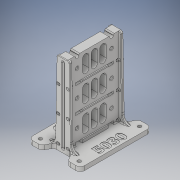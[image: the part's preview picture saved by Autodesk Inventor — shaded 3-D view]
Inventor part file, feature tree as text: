
AUTODESK INVENTOR PART (.ipt)
format: ipt  version: 2018.3 (Build 223284000, 284)  size: 1,960,960 bytes
history: native  units: in
note: dims shown in document units (in); Inventor stores cm internally (conversion verified against a paired STEP export)
features: extrude x12, sketch x11, fillet x9, mirror x4, chamfer x3, hole x2, emboss x2, pattern_linear x1, pattern_circular x1, revolve x1
ambient origin geometry x8: Origin, YZ Plane, XZ Plane, XY Plane, X Axis, Y Axis, Z Axis, Center Point
bodies: Solid1 (feature_tree)
feature tree (46):
  sketch  "Sketch1"  dims[d0=0.5in d1=3.0in]
  extrude  "Extrusion1"  Depth=3.0in
  sketch  "Sketch2"  dims[d2=4.779in d3=0.25in]
  extrude  "Extrusion2"  Depth=0.25in
  mirror  "Mirror1"
  hole  "Hole1"  [1 undecoded]
  extrude  "Extrusion3"  Depth=2.771in
  pattern_linear  "Rectangular Pattern1"  Count1=3 Spacing1=1.5in
  chamfer  "Chamfer1"  Distance=0.1562in
  fillet  "Fillet1"  Radius=1.0in
  extrude  "Extrusion4"  Depth=0.3937in
  extrude  "Extrusion5"  Depth=0.0625in TaperAngle=0.0deg
  chamfer  "Chamfer2"  Distance=1.1811in
  mirror  "Mirror2"
  fillet  "Fillet2"  Radius=0.0312in
  sketch  "Sketch3"  dims[d4=0.5in d5=3.125in d6=0.0in]
  sketch  "Sketch4"  dims[d7=2.0in d8=2.771in]
  extrude  "Extrusion6"  Depth=0.0625in
  extrude  "Extrusion9"  Depth=0.0625in
  hole  "Hole2"  [1 undecoded]
  fillet  "Fillet3"  Radius=0.1in
  extrude  "Extrusion7"  Depth=0.3937in
  extrude  "Extrusion8"  Depth=0.0625in
  mirror  "Mirror3"
  fillet  "Fillet4"  Radius=0.0625in
  fillet  "Fillet6"  Radius=0.0625in
  emboss  "Emboss1"
  sketch  "Sketch8"  dims[d21=0.125in]
  extrude  "Extrusion10"  Depth=0.0625in
  extrude  "Extrusion11"  Depth=0.0625in TaperAngle=45.0deg
  extrude  "Extrusion12"  Depth=0.0625in
  chamfer  "Chamfer3"  Distance=4.125in
  emboss  "Emboss2"
  pattern_circular  "Circular Pattern1"  [2 undecoded]
  revolve  "Revolution1"  [1 undecoded]
  mirror  "Mirror4"
  fillet  "Fillet8"  Radius=3.125in
  fillet  "Fillet9"  Radius=4.25in
  fillet  "Fillet7"  Radius=2.5in
  fillet  "Fillet5"  Radius=3.75in
  sketch  "Sketch5"  dims[d9=1.2in]
  sketch  "Sketch6"  dims[d11=0.25in d12=1.1811in d14=1.5in d15=0.3937in d17=1.0in]
  sketch  "Sketch7"  dims[d20=0.5in]
  sketch  "Sketch9"  dims[d22=0.2in d23=0.1562in d24=0.0in]
  sketch  "Sketch10"  dims[d25=0.164in d26=0.328in d27=0.375in d28=0.25in d29=0.5635in d30=0.484in d31=0.8108in d32=1.0in]
  sketch  "Sketch11"  dims[d33=0.375in d34=1.1811in d36=1.5in d37=0.3937in d39=1.0in d41=2.5in d42=0.0in d43=1.1811in d45=0.5in d46=0.0312in d47=0.125in d48=45.0deg d49=0.125in d50=0.375in d52=0.01in d53=2.0in d54=0.1in d55=1.1811in d57=1.5in d58=0.3937in d60=1.0in d62=0.01in d63=0.0625in d64=0.0in d65=0.0625in d66=0.0in d67=0.1875in d68=0.0625in d69=0.125in d70=45.0deg d72=3.0in d73=4.125in d74=2.25in d75=3.5in d76=3.125in d77=4.25in d78=2.5in d79=3.75in d80=0.0625in d81=0.0in d82=0.201in d83=0.328in d84=0.375in d85=0.25in d86=0.5635in d87=0.484in d88=0.8108in d89=0.25in d90=0.15in d91=0.075in d92=0.5in d93=0.7874in d95=1.5in d96=0.3937in d98=1.0in d100=0.0625in d101=0.0in d102=0.5in d103=0.0625in d104=0.7874in d106=1.5in d107=0.3937in d109=1.0in d111=0.0625in d112=0.0in d113=0.0312in d114=0.125in d115=1.5in d116=60.0deg d117=0.5in d118=0.0625in d119=0.0in d120=0.7874in d122=1.5in d123=0.3937in d125=1.0in d127=0.0625in d128=0.0312in d129=0.0157in d130=0.0in d131=0.152in d132=1.358in d133=1.358in d134=0.679in d135=0.5in d136=4.9375in d137=0.0in d138=0.0625in d139=1.365in d140=1.365in d141=0.25in d142=4.9375in d143=0.0in d144=0.625in d145=0.0in d146=0.0625in d147=0.125in d148=45.0deg d149=0.0157in d150=0.0in d151=0.7874in d152=360.0deg d154=0.25in d155=0.25in d156=0.125in d157=90.0deg d158=0.0625in d159=0.0625in]
note: 5 required parameter values undecoded (feature->parameter linkage not recoverable at this tier; creation-order binding heuristic only, values carry confidence <= 0.55)